# Revit family: Flap_LivingDivaniBIM
name_source: partatom
category: Arredi
revit_build: Autodesk Revit 2017 (Build: 20190508_0315(x64)
units: mm (PartAtom-declared; Revit-internal decimal feet)

## family parameters
Basato su piano di lavoro = No
Condiviso = No
Numero OmniClass = 23.40.20.14
Punto di calcolo locali = No
Sempre verticale = Sì
Taglio con vuoti quando caricato = No
Titolo OmniClass = Residential Furniture

## types (4) — shared parameters
Materiale struttura = Metallo LivingDivani
Modello = Flap
Produttore = Living Divani
URL = www.livingdivani.it
materiale plastica = plastica
materiale struttura secondaria = Metallo LivingDivani 2
zero-valued in all types: Costo

## per-type parameters (varying)
| type | Codice Prodotto | Ovale_piedini | Ovale_porte | Ovale_struttura | Quadrato_piedini | Quadrato_porte | Quadrato_struttura | Rettangolare_piedini | Rettangolare_porte | Rettangolare_struttura | Rotondo_piedini | Rotondo_porte | Rotondo_struttura |
| Flap Ovale | FLAV180O | Sì | Sì | Sì | No | No | No | No | No | No | No | No | No |
| Flap quadrato | FLAV090Q | No | No | No | Sì | Sì | Sì | No | No | No | No | No | No |
| Flap rettangolare | FLAV180RT | No | No | No | No | No | No | Sì | Sì | Sì | No | No | No |
| Flap rotondo | FLAV070R | No | No | No | No | No | No | No | No | No | Sì | Sì | Sì |
